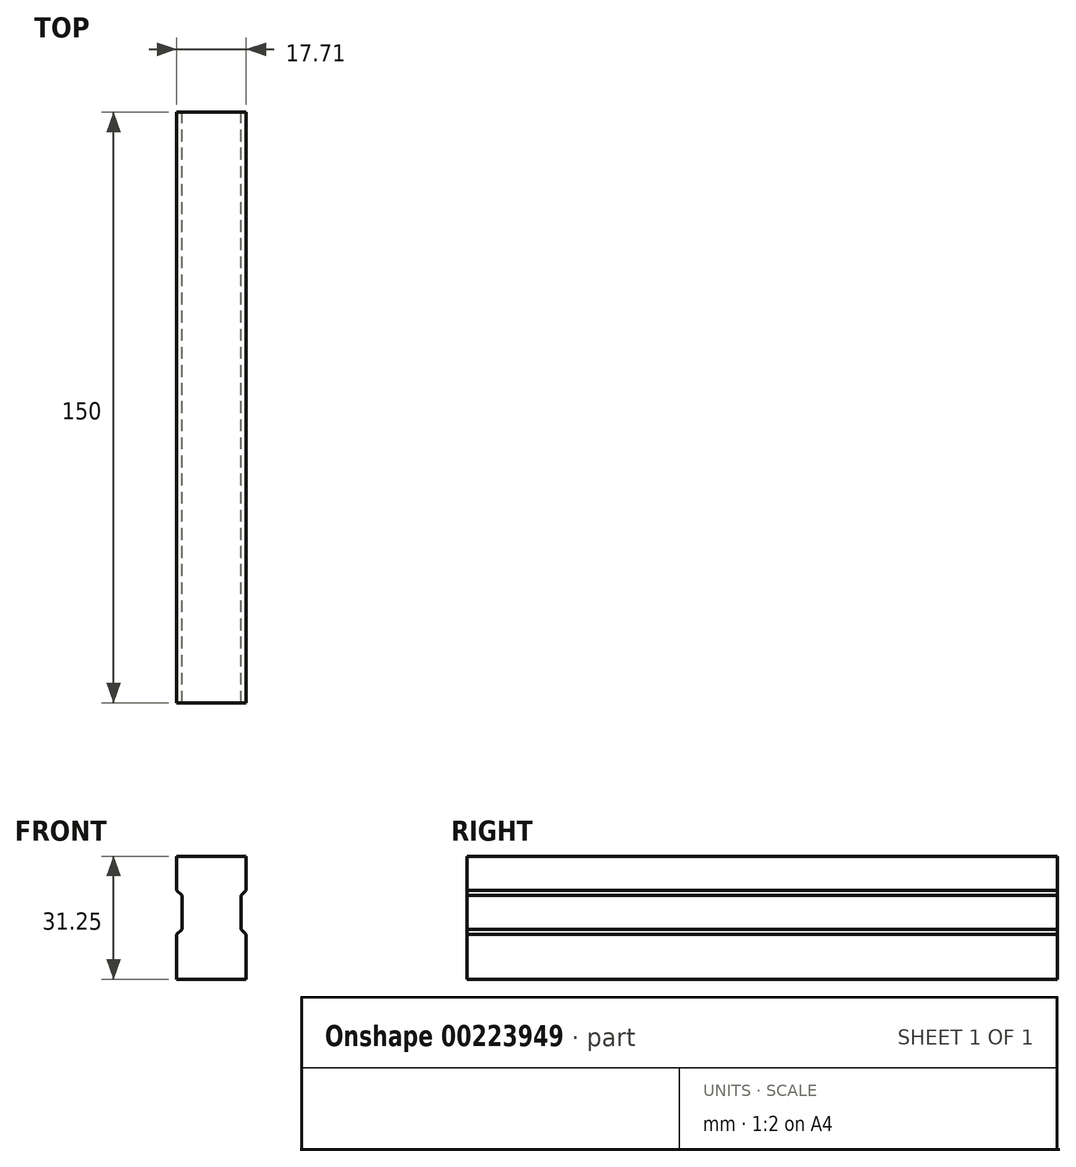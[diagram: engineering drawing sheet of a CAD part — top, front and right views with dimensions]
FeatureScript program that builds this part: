
annotation { "Feature Type Name" : "Feature", "Feature Type Description" : "" }
export const myFeature = defineFeature(function(context is Context, id is Id, definition is map)
    precondition{}
    {
        {
            var Q0;
            Q0=qCreatedBy(makeId("Front.planeOp"),FACE);
            var sketch = newSketch(context, id + "F0", { "sketchPlane" : qUnion([Q0])});
            skLineSegment(sketch, "E0.bottom", {"start": v(0, 0) * mm, "end": v(17.7, 0) * mm, "construction": true});
            skLineSegment(sketch, "E0.top", {"start": v(0, 31.25) * mm, "end": v(17.7, 31.25) * mm, "construction": true});
            skLineSegment(sketch, "E0.left", {"start": v(0, 0) * mm, "end": v(0, 31.25) * mm, "construction": true});
            skLineSegment(sketch, "E0.right", {"start": v(17.7, 0) * mm, "end": v(17.7, 31.25) * mm, "construction": true});
            skLineSegment(sketch, "E1", {"start": v(8.85, 31.25) * mm, "end": v(8.85, 0) * mm, "construction": true});
            skLineSegment(sketch, "E2", {"start": v(8.85, 0) * mm, "end": v(0, 0) * mm});
            skLineSegment(sketch, "E3", {"start": v(0, 11.35) * mm, "end": v(1.35, 12.6) * mm});
            skLineSegment(sketch, "E4", {"start": v(1.35, 12.6) * mm, "end": v(1.35, 21.35) * mm});
            skLineSegment(sketch, "E5", {"start": v(1.35, 21.35) * mm, "end": v(0, 22.6) * mm});
            skLineSegment(sketch, "E6", {"start": v(0, 22.6) * mm, "end": v(0, 31.25) * mm});
            skLineSegment(sketch, "E7", {"start": v(8.85, 31.25) * mm, "end": v(0, 31.25) * mm});
            skLineSegment(sketch, "E8", {"start": v(0, 0) * mm, "end": v(0, 11.35) * mm});
            skLineSegment(sketch, "E9.MirrorCS", {"start": v(16.35, 21.35) * mm, "end": v(17.7, 22.6) * mm});
            skLineSegment(sketch, "E10.MirrorCS", {"start": v(17.7, 11.35) * mm, "end": v(16.35, 12.6) * mm});
            skLineSegment(sketch, "E11.MirrorCS", {"start": v(17.7, 0) * mm, "end": v(17.7, 11.35) * mm});
            skLineSegment(sketch, "E12.MirrorCS", {"start": v(8.85, 31.25) * mm, "end": v(17.7, 31.25) * mm});
            skLineSegment(sketch, "E13.MirrorCS", {"start": v(8.85, 0) * mm, "end": v(17.7, 0) * mm});
            skLineSegment(sketch, "E14.MirrorCS", {"start": v(16.35, 12.6) * mm, "end": v(16.35, 21.35) * mm});
            skLineSegment(sketch, "E15.MirrorCS", {"start": v(17.7, 22.6) * mm, "end": v(17.7, 31.25) * mm});
            skSolve(sketch);
        }
        {
            var Q0;
            Q0=makeQuery(id+"F0.imprint","IMPRINT",FACE,{"disambiguationData":[TD([[makeQuery(id+"F0.imprint","IMPRINT",EDGE,{"derivedFrom":sQuery(id+"F0.wireOp",EDGE,"E2")}),-1.0]])]});
            extrude(context, id + "F1", {"entities" : qUnion([Q0]), "depth" : 150 * mm});
        }
    });
